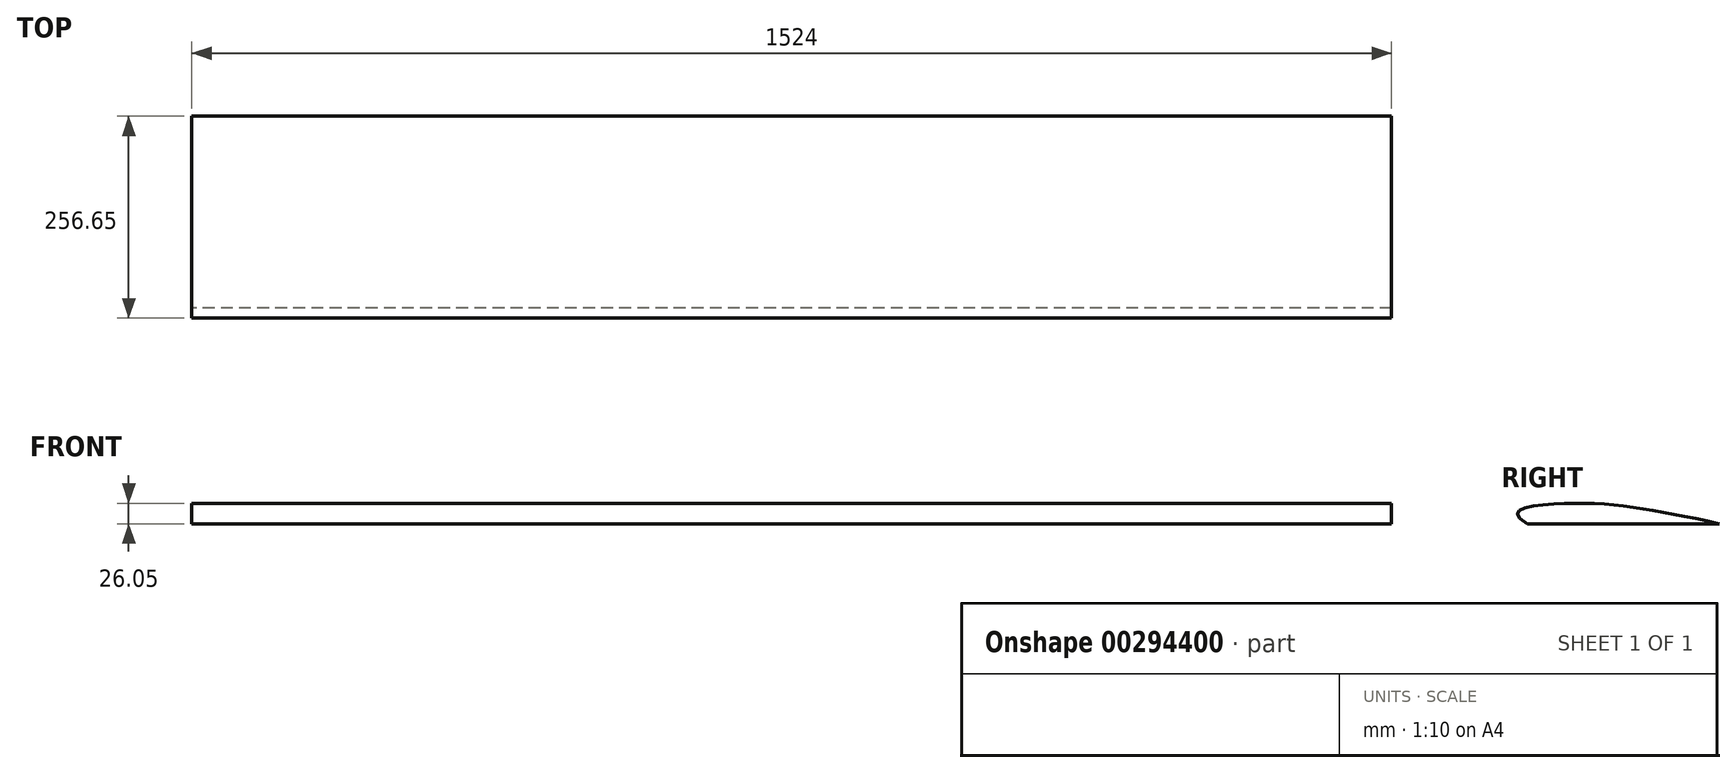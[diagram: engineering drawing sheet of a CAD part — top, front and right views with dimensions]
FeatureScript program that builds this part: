
annotation { "Feature Type Name" : "Feature", "Feature Type Description" : "" }
export const myFeature = defineFeature(function(context is Context, id is Id, definition is map)
    precondition{}
    {
        {
            var Q0;
            Q0=qCreatedBy(makeId("Right.planeOp"),FACE);
            var sketch = newSketch(context, id + "F0", { "sketchPlane" : qUnion([Q0])});
            skLineSegment(sketch, "E0", {"start": v(-43.35, 0) * mm, "end": v(200.49, 0) * mm});
            skFitSpline(sketch, "E1", {"points": [v(-43.35, 0) * mm, v(-6.03, 25.4) * mm, v(200.49, 0) * mm], "startDerivative": vector(-310.82, 178.28) * mm, "endDerivative": vector(365.92, -77.21) * mm});
            skSolve(sketch);
        }
        {
            var Q0;
            Q0 = qSketchRegion(id + "F0", true);
            extrude(context, id + "F1", {"entities" : qUnion([Q0]), "depth" : 1524 * mm, "offsetDistance" : 25.4 * mm});
        }
    });
